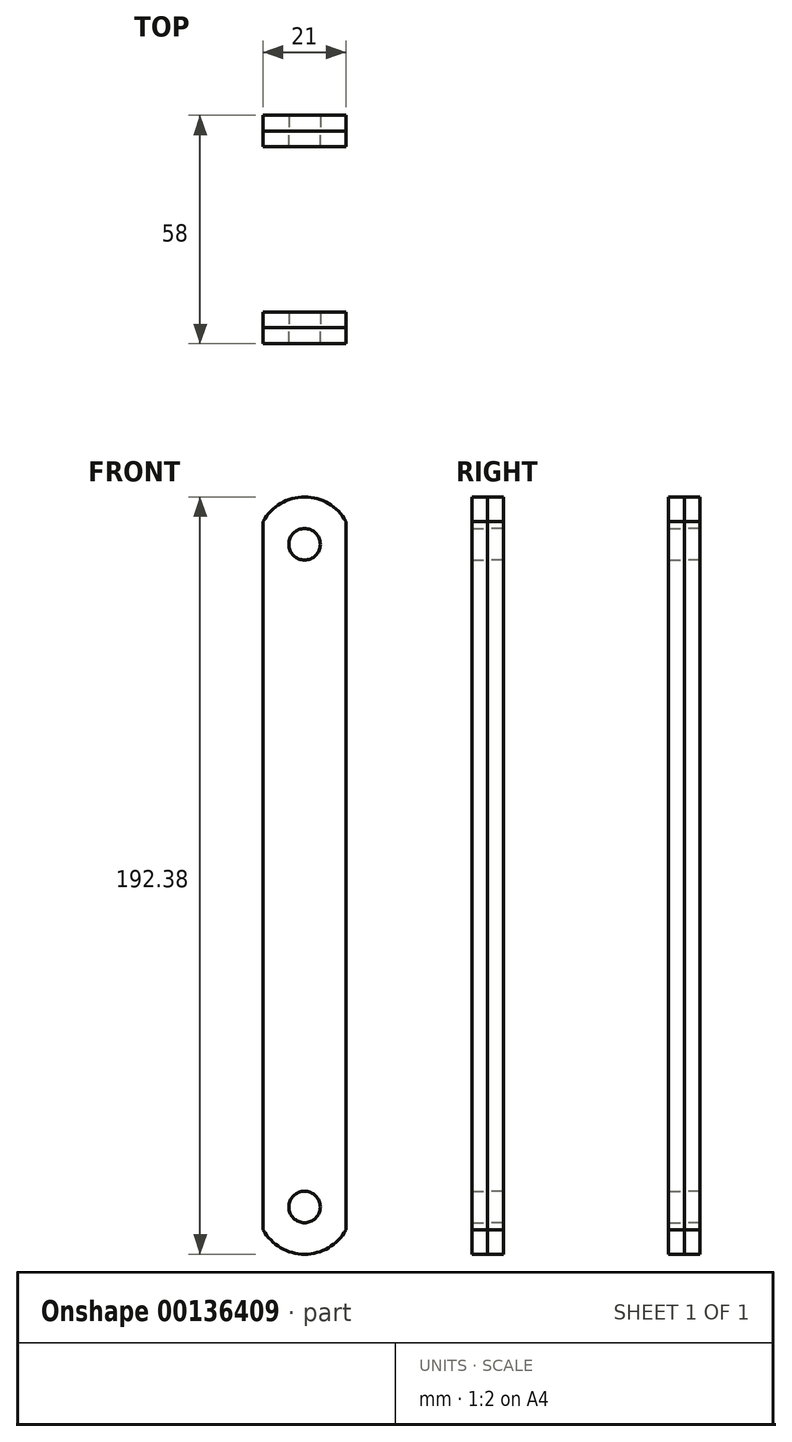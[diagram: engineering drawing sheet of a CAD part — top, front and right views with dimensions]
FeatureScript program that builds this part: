
annotation { "Feature Type Name" : "Feature", "Feature Type Description" : "" }
export const myFeature = defineFeature(function(context is Context, id is Id, definition is map)
    precondition{}
    {
        {
            var Q0;
            Q0=qCreatedBy(makeId("Front.planeOp"),FACE);
            var sketch = newSketch(context, id + "F0", { "sketchPlane" : qUnion([Q0])});
            skLineSegment(sketch, "E0", {"start": v(-10.5, 90) * mm, "end": v(-10.5, -90) * mm});
            skLineSegment(sketch, "E1.MirrorCS", {"start": v(10.5, 90) * mm, "end": v(10.5, -90) * mm});
            skArc(sketch, "E2", {"start": v(10.5, 90) * mm, "mid": v(0, 96.2) * mm, "end": v(-10.5, 90) * mm});
            skArc(sketch, "E3.MirrorCS", {"start": v(10.5, -90) * mm, "mid": v(0, -96.2) * mm, "end": v(-10.5, -90) * mm});
            skCircle(sketch, "E4", {"center": v(0, 84.2) * mm, "radius": 4 * mm});
            skCircle(sketch, "E5", {"center": v(0, -84.2) * mm, "radius": 4 * mm});
            skSolve(sketch);
        }
        {
            var Q0;
            Q0 = qSketchRegion(id + "F0", true);
            extrude(context, id + "F1", {"entities" : qUnion([Q0]), "depth" : 4 * mm});
        }
        {
            var Q0;
            Q0=makeQuery(id+"F1.opExtrude","SWEPT_BODY",BODY,{"disambiguationData":[OSD([sQuery(id+"F0.wireOp",EDGE,"E0"),sQuery(id+"F0.wireOp",EDGE,"E1.MirrorCS"),sQuery(id+"F0.wireOp",EDGE,"E2"),sQuery(id+"F0.wireOp",EDGE,"E3.MirrorCS"),sQuery(id+"F0.wireOp",EDGE,"E4"),sQuery(id+"F0.wireOp",EDGE,"E5")])]});
            var Q1;
            Q1=qCreatedBy(makeId("Front.planeOp"),FACE);
            mirror(context, id + "F2", {"entities" : qUnion([Q0]), "mirrorPlane" : qUnion([Q1])});
        }
        {
            var Q0;
            Q0=qCreatedBy(makeId("Front.planeOp"),FACE);
            cPlane(context, id + "F3", {"entities" : qUnion([Q0]), "cplaneType" : CPlaneType.OFFSET, "offset" : 25 * mm, "width" : 150 * mm, "height" : 150 * mm});
        }
        {
            var Q0;
            Q0=makeQuery(id+"F2.opPattern","COPY",BODY,{"derivedFrom":makeQuery(id+"F1.opExtrude","SWEPT_BODY",BODY,{"disambiguationData":[OSD([sQuery(id+"F0.wireOp",EDGE,"E0"),sQuery(id+"F0.wireOp",EDGE,"E1.MirrorCS"),sQuery(id+"F0.wireOp",EDGE,"E2"),sQuery(id+"F0.wireOp",EDGE,"E3.MirrorCS"),sQuery(id+"F0.wireOp",EDGE,"E4"),sQuery(id+"F0.wireOp",EDGE,"E5")])]}),"instanceName":"1"});
            var Q1;
            Q1=makeQuery(id+"F1.opExtrude","SWEPT_BODY",BODY,{"disambiguationData":[OSD([sQuery(id+"F0.wireOp",EDGE,"E0"),sQuery(id+"F0.wireOp",EDGE,"E1.MirrorCS"),sQuery(id+"F0.wireOp",EDGE,"E2"),sQuery(id+"F0.wireOp",EDGE,"E3.MirrorCS"),sQuery(id+"F0.wireOp",EDGE,"E4"),sQuery(id+"F0.wireOp",EDGE,"E5")])]});
            var Q2;
            Q2=qCreatedBy(id+"F3.planeOp",FACE);
            mirror(context, id + "F4", {"entities" : qUnion([Q0, Q1]), "mirrorPlane" : qUnion([Q2])});
        }
    });
